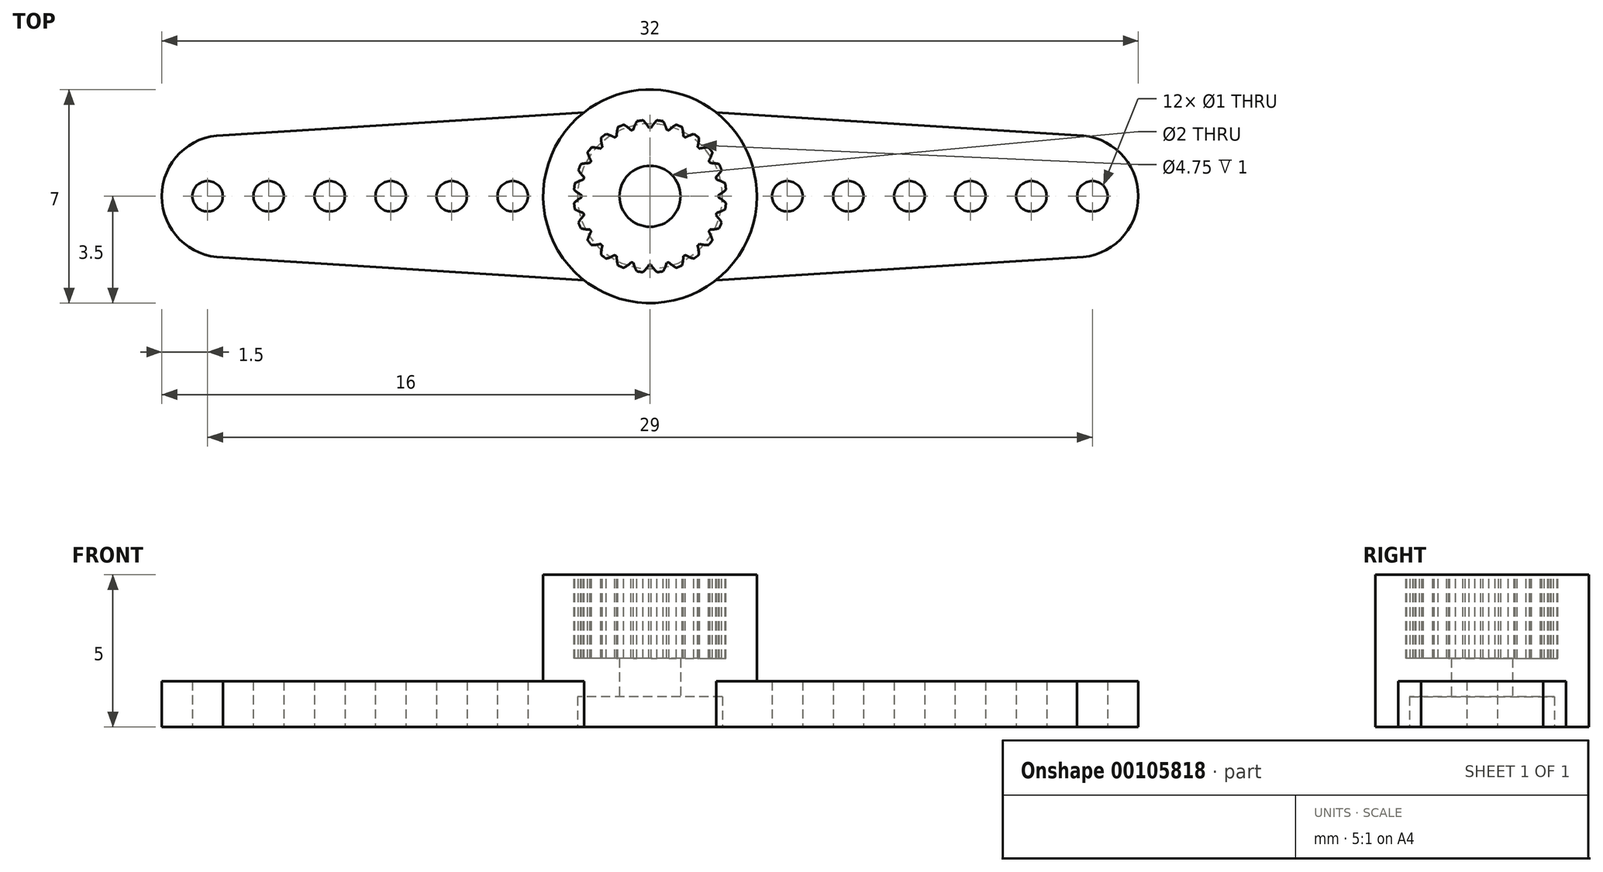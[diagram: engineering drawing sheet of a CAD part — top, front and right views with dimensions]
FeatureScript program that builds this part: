
annotation { "Feature Type Name" : "Feature", "Feature Type Description" : "" }
export const myFeature = defineFeature(function(context is Context, id is Id, definition is map)
    precondition{}
    {
        {
            var Q0;
            Q0=qCreatedBy(makeId("Top.planeOp"),FACE);
            var sketch = newSketch(context, id + "F0", { "sketchPlane" : qUnion([Q0])});
            skCircle(sketch, "E0", {"center": v(0, 0) * mm, "radius": 3.5 * mm});
            skCircle(sketch, "E1", {"center": v(-14, 0) * mm, "radius": 2 * mm});
            skLineSegment(sketch, "E2", {"start": v(-14, 2) * mm, "end": v(-2.17, 2.75) * mm});
            skLineSegment(sketch, "E3", {"start": v(-14, -2) * mm, "end": v(-2.17, -2.75) * mm});
            skCircle(sketch, "E4", {"center": v(0, 0) * mm, "radius": 1 * mm});
            skCircle(sketch, "E5", {"center": v(-14.5, 0) * mm, "radius": 0.5 * mm});
            skLineSegment(sketch, "E6", {"start": v(-16.68, 0) * mm, "end": v(5.78, 0) * mm, "construction": true});
            skCircle(sketch, "E7.1.0.0", {"center": v(-12.5, 0) * mm, "radius": 0.5 * mm});
            skCircle(sketch, "E7.2.0.0", {"center": v(-10.5, 0) * mm, "radius": 0.5 * mm});
            skLineSegment(sketch, "E7.direction1", {"start": v(-14.5, 0) * mm, "end": v(-12.5, 0) * mm, "construction": true});
            skCircle(sketch, "E8.0.3.0", {"center": v(-8.5, 0) * mm, "radius": 0.5 * mm});
            skCircle(sketch, "E8.0.4.0", {"center": v(-6.5, 0) * mm, "radius": 0.5 * mm});
            skCircle(sketch, "E8.0.5.0", {"center": v(-4.5, 0) * mm, "radius": 0.5 * mm});
            skSolve(sketch);
        }
        {
            var Q0;
            {var subQ6=sQuery(id+"F0.wireOp",EDGE,"E2");Q0=makeQuery(id+"F0.imprint","IMPRINT",FACE,{"disambiguationData":[TD([[makeQuery(id+"F0.imprint","IMPRINT",EDGE,{"derivedFrom":subQ6}),-1.0]])]});}
            var Q1;
            Q1=makeQuery(id+"F0.imprint","IMPRINT",FACE,{"disambiguationData":[TD([[makeQuery(id+"F0.imprint","IMPRINT",EDGE,{"derivedFrom":sQuery(id+"F0.wireOp",EDGE,"11ce5147-8903-4a82-81a3-89551e99495c")}),-1.0]])]});
            var Q2;
            Q2=makeQuery(id+"F0.imprint","IMPRINT",FACE,{"disambiguationData":[TD([[makeQuery(id+"F0.imprint","IMPRINT",EDGE,{"derivedFrom":sQuery(id+"F0.wireOp",EDGE,"E4")}),-1.0]])]});
            var Q3;
            Q3=makeQuery(id+"F0.imprint","IMPRINT",FACE,{"disambiguationData":[TD([[makeQuery(id+"F0.imprint","IMPRINT",EDGE,{"derivedFrom":sQuery(id+"F0.wireOp",EDGE,"E5")}),-1.0]])]});
            extrude(context, id + "F1", {"entities" : qUnion([Q0, Q1, Q2, Q3]), "depth" : 1.5 * mm});
        }
        {
            var Q0;
            Q0=makeQuery(id+"F0.imprint","IMPRINT",FACE,{"disambiguationData":[TD([[makeQuery(id+"F0.imprint","IMPRINT",EDGE,{"derivedFrom":sQuery(id+"F0.wireOp",EDGE,"E4")}),-1.0]])]});
            extrude(context, id + "F2", {"entities" : qUnion([Q0]), "operationType" : NewBodyOperationType.ADD, "depth" : 5 * mm});
        }
        {
            var Q0;
            Q0=makeQuery(id+"F0.imprint","IMPRINT",FACE,{"disambiguationData":[TD([[makeQuery(id+"F0.imprint","IMPRINT",EDGE,{"derivedFrom":sQuery(id+"F0.wireOp",EDGE,"E4")}),-1.0]])]});
            var sketch = newSketch(context, id + "F3", { "sketchPlane" : qUnion([Q0])});
            skCircle(sketch, "E9", {"center": v(0, 0) * mm, "radius": 2.37 * mm});
            skSolve(sketch);
        }
        {
            var Q0;
            Q0=qSketchRegion(id+"F3",true);
            extrude(context, id + "F4", {"entities" : qUnion([Q0]), "operationType" : NewBodyOperationType.REMOVE, "depth" : 1 * mm});
        }
        {
            var Q0;
            Q0=makeQuery(id+"F2.opExtrude","CAP_FACE",FACE,{"disambiguationData":[OSD([sQuery(id+"F0.wireOp",EDGE,"E0"),sQuery(id+"F0.wireOp",EDGE,"E4")])],"isStart":false});
            var sketch = newSketch(context, id + "F5", { "sketchPlane" : qUnion([Q0])});
            skCircle(sketch, "E10", {"center": v(0, 0) * mm, "radius": 2.25 * mm});
            skCircle(sketch, "E11", {"center": v(0, 0) * mm, "radius": 2.5 * mm, "construction": true});
            skLineSegment(sketch, "E12", {"start": v(0, 0) * mm, "end": v(0.98, 3.66) * mm, "construction": true});
            skLineSegment(sketch, "E13", {"start": v(0, 0) * mm, "end": v(2.5, 4.33) * mm, "construction": true});
            skArc(sketch, "E14", {"start": v(0.23, 2.49) * mm, "mid": v(0.12, 2.38) * mm, "end": v(0.04, 2.25) * mm});
            skArc(sketch, "E15", {"start": v(0.54, 2.18) * mm, "mid": v(0.5, 2.33) * mm, "end": v(0.43, 2.46) * mm});
            skArc(sketch, "E16", {"start": v(0.43, 2.46) * mm, "mid": v(0.33, 2.48) * mm, "end": v(0.23, 2.49) * mm});
            skCircle(sketch, "E17.2.0", {"center": v(0, 0) * mm, "radius": 2.25 * mm, "construction": true});
            skArc(sketch, "E18.1.1", {"start": v(-0.43, 2.46) * mm, "mid": v(-0.5, 2.33) * mm, "end": v(-0.54, 2.18) * mm});
            skArc(sketch, "E18.1.2", {"start": v(-0.23, 2.49) * mm, "mid": v(-0.33, 2.48) * mm, "end": v(-0.43, 2.46) * mm});
            skArc(sketch, "E18.1.3", {"start": v(-0.04, 2.25) * mm, "mid": v(-0.12, 2.38) * mm, "end": v(-0.23, 2.49) * mm});
            skArc(sketch, "E18.2.1", {"start": v(-1.05, 2.27) * mm, "mid": v(-1.1, 2.12) * mm, "end": v(-1.1, 1.97) * mm});
            skArc(sketch, "E18.2.2", {"start": v(-0.86, 2.35) * mm, "mid": v(-0.96, 2.3) * mm, "end": v(-1.05, 2.27) * mm});
            skArc(sketch, "E18.2.3", {"start": v(-0.62, 2.16) * mm, "mid": v(-0.73, 2.26) * mm, "end": v(-0.86, 2.35) * mm});
            skArc(sketch, "E19.2.3.0", {"start": v(-1.6, 1.92) * mm, "mid": v(-1.6, 1.77) * mm, "end": v(-1.56, 1.62) * mm});
            skArc(sketch, "E19.6.3.0", {"start": v(-1.44, 2.04) * mm, "mid": v(-1.52, 1.98) * mm, "end": v(-1.6, 1.92) * mm});
            skArc(sketch, "E19.10.3.0", {"start": v(-1.16, 1.93) * mm, "mid": v(-1.3, 2) * mm, "end": v(-1.44, 2.04) * mm});
            skArc(sketch, "E19.2.4.0", {"start": v(-2.04, 1.44) * mm, "mid": v(-2, 1.3) * mm, "end": v(-1.93, 1.16) * mm});
            skArc(sketch, "E19.6.4.0", {"start": v(-1.92, 1.6) * mm, "mid": v(-1.98, 1.52) * mm, "end": v(-2.04, 1.44) * mm});
            skArc(sketch, "E19.10.4.0", {"start": v(-1.62, 1.56) * mm, "mid": v(-1.77, 1.6) * mm, "end": v(-1.92, 1.6) * mm});
            skArc(sketch, "E19.2.5.0", {"start": v(-2.35, 0.86) * mm, "mid": v(-2.27, 0.73) * mm, "end": v(-2.16, 0.62) * mm});
            skArc(sketch, "E19.6.5.0", {"start": v(-2.27, 1.05) * mm, "mid": v(-2.3, 0.96) * mm, "end": v(-2.35, 0.86) * mm});
            skArc(sketch, "E19.10.5.0", {"start": v(-1.97, 1.1) * mm, "mid": v(-2.12, 1.08) * mm, "end": v(-2.27, 1.05) * mm});
            skArc(sketch, "E19.2.6.0", {"start": v(-2.49, 0.23) * mm, "mid": v(-2.38, 0.12) * mm, "end": v(-2.25, 0.04) * mm});
            skArc(sketch, "E19.6.6.0", {"start": v(-2.46, 0.43) * mm, "mid": v(-2.48, 0.33) * mm, "end": v(-2.49, 0.23) * mm});
            skArc(sketch, "E19.10.6.0", {"start": v(-2.18, 0.54) * mm, "mid": v(-2.33, 0.5) * mm, "end": v(-2.46, 0.43) * mm});
            skArc(sketch, "E19.2.7.0", {"start": v(-2.46, -0.43) * mm, "mid": v(-2.33, -0.5) * mm, "end": v(-2.18, -0.54) * mm});
            skArc(sketch, "E19.6.7.0", {"start": v(-2.49, -0.22) * mm, "mid": v(-2.48, -0.33) * mm, "end": v(-2.46, -0.43) * mm});
            skArc(sketch, "E19.10.7.0", {"start": v(-2.25, -0.04) * mm, "mid": v(-2.38, -0.12) * mm, "end": v(-2.49, -0.22) * mm});
            skArc(sketch, "E19.2.8.0", {"start": v(-2.27, -1.05) * mm, "mid": v(-2.12, -1.1) * mm, "end": v(-1.97, -1.1) * mm});
            skArc(sketch, "E19.6.8.0", {"start": v(-2.35, -0.86) * mm, "mid": v(-2.3, -0.96) * mm, "end": v(-2.27, -1.05) * mm});
            skArc(sketch, "E19.10.8.0", {"start": v(-2.16, -0.62) * mm, "mid": v(-2.26, -0.73) * mm, "end": v(-2.35, -0.86) * mm});
            skArc(sketch, "E19.2.9.0", {"start": v(-1.92, -1.6) * mm, "mid": v(-1.77, -1.6) * mm, "end": v(-1.62, -1.56) * mm});
            skArc(sketch, "E19.6.9.0", {"start": v(-2.04, -1.44) * mm, "mid": v(-1.98, -1.52) * mm, "end": v(-1.92, -1.6) * mm});
            skArc(sketch, "E19.10.9.0", {"start": v(-1.93, -1.16) * mm, "mid": v(-2, -1.3) * mm, "end": v(-2.04, -1.44) * mm});
            skArc(sketch, "E19.2.10.0", {"start": v(-1.44, -2.04) * mm, "mid": v(-1.3, -2) * mm, "end": v(-1.16, -1.93) * mm});
            skArc(sketch, "E19.6.10.0", {"start": v(-1.6, -1.92) * mm, "mid": v(-1.52, -1.98) * mm, "end": v(-1.44, -2.04) * mm});
            skArc(sketch, "E19.10.10.0", {"start": v(-1.56, -1.62) * mm, "mid": v(-1.6, -1.77) * mm, "end": v(-1.6, -1.92) * mm});
            skArc(sketch, "E19.2.11.0", {"start": v(-0.86, -2.35) * mm, "mid": v(-0.73, -2.27) * mm, "end": v(-0.62, -2.16) * mm});
            skArc(sketch, "E19.6.11.0", {"start": v(-1.05, -2.27) * mm, "mid": v(-0.96, -2.3) * mm, "end": v(-0.86, -2.35) * mm});
            skArc(sketch, "E19.10.11.0", {"start": v(-1.1, -1.97) * mm, "mid": v(-1.08, -2.12) * mm, "end": v(-1.05, -2.27) * mm});
            skArc(sketch, "E19.2.12.0", {"start": v(-0.23, -2.49) * mm, "mid": v(-0.12, -2.38) * mm, "end": v(-0.04, -2.25) * mm});
            skArc(sketch, "E19.6.12.0", {"start": v(-0.43, -2.46) * mm, "mid": v(-0.33, -2.48) * mm, "end": v(-0.23, -2.49) * mm});
            skArc(sketch, "E19.10.12.0", {"start": v(-0.54, -2.18) * mm, "mid": v(-0.5, -2.33) * mm, "end": v(-0.43, -2.46) * mm});
            skArc(sketch, "E19.2.13.0", {"start": v(0.43, -2.46) * mm, "mid": v(0.5, -2.33) * mm, "end": v(0.54, -2.18) * mm});
            skArc(sketch, "E19.6.13.0", {"start": v(0.22, -2.49) * mm, "mid": v(0.33, -2.48) * mm, "end": v(0.43, -2.46) * mm});
            skArc(sketch, "E19.10.13.0", {"start": v(0.04, -2.25) * mm, "mid": v(0.12, -2.38) * mm, "end": v(0.23, -2.49) * mm});
            skArc(sketch, "E19.2.14.0", {"start": v(1.05, -2.27) * mm, "mid": v(1.1, -2.12) * mm, "end": v(1.1, -1.97) * mm});
            skArc(sketch, "E19.6.14.0", {"start": v(0.86, -2.35) * mm, "mid": v(0.96, -2.3) * mm, "end": v(1.05, -2.27) * mm});
            skArc(sketch, "E19.10.14.0", {"start": v(0.62, -2.16) * mm, "mid": v(0.73, -2.26) * mm, "end": v(0.86, -2.35) * mm});
            skArc(sketch, "E19.2.15.0", {"start": v(1.6, -1.92) * mm, "mid": v(1.6, -1.77) * mm, "end": v(1.56, -1.62) * mm});
            skArc(sketch, "E19.6.15.0", {"start": v(1.44, -2.04) * mm, "mid": v(1.52, -1.98) * mm, "end": v(1.6, -1.92) * mm});
            skArc(sketch, "E19.10.15.0", {"start": v(1.16, -1.93) * mm, "mid": v(1.3, -2) * mm, "end": v(1.44, -2.04) * mm});
            skArc(sketch, "E19.2.16.0", {"start": v(2.04, -1.44) * mm, "mid": v(2, -1.3) * mm, "end": v(1.93, -1.16) * mm});
            skArc(sketch, "E19.6.16.0", {"start": v(1.92, -1.6) * mm, "mid": v(1.98, -1.52) * mm, "end": v(2.04, -1.44) * mm});
            skArc(sketch, "E19.10.16.0", {"start": v(1.62, -1.56) * mm, "mid": v(1.77, -1.6) * mm, "end": v(1.92, -1.6) * mm});
            skArc(sketch, "E19.2.17.0", {"start": v(2.35, -0.86) * mm, "mid": v(2.27, -0.73) * mm, "end": v(2.16, -0.62) * mm});
            skArc(sketch, "E19.6.17.0", {"start": v(2.27, -1.05) * mm, "mid": v(2.3, -0.96) * mm, "end": v(2.35, -0.86) * mm});
            skArc(sketch, "E19.10.17.0", {"start": v(1.97, -1.1) * mm, "mid": v(2.12, -1.08) * mm, "end": v(2.27, -1.05) * mm});
            skArc(sketch, "E19.2.18.0", {"start": v(2.49, -0.23) * mm, "mid": v(2.38, -0.12) * mm, "end": v(2.25, -0.04) * mm});
            skArc(sketch, "E19.6.18.0", {"start": v(2.46, -0.43) * mm, "mid": v(2.48, -0.33) * mm, "end": v(2.49, -0.23) * mm});
            skArc(sketch, "E19.10.18.0", {"start": v(2.18, -0.54) * mm, "mid": v(2.33, -0.5) * mm, "end": v(2.46, -0.43) * mm});
            skArc(sketch, "E19.2.19.0", {"start": v(2.46, 0.43) * mm, "mid": v(2.33, 0.5) * mm, "end": v(2.18, 0.54) * mm});
            skArc(sketch, "E19.6.19.0", {"start": v(2.49, 0.22) * mm, "mid": v(2.48, 0.33) * mm, "end": v(2.46, 0.43) * mm});
            skArc(sketch, "E19.10.19.0", {"start": v(2.25, 0.04) * mm, "mid": v(2.38, 0.12) * mm, "end": v(2.49, 0.22) * mm});
            skArc(sketch, "E19.2.20.0", {"start": v(2.27, 1.05) * mm, "mid": v(2.12, 1.1) * mm, "end": v(1.97, 1.1) * mm});
            skArc(sketch, "E19.6.20.0", {"start": v(2.35, 0.86) * mm, "mid": v(2.3, 0.96) * mm, "end": v(2.27, 1.05) * mm});
            skArc(sketch, "E19.10.20.0", {"start": v(2.16, 0.62) * mm, "mid": v(2.26, 0.73) * mm, "end": v(2.35, 0.86) * mm});
            skArc(sketch, "E19.2.21.0", {"start": v(1.92, 1.6) * mm, "mid": v(1.77, 1.6) * mm, "end": v(1.62, 1.56) * mm});
            skArc(sketch, "E19.6.21.0", {"start": v(2.04, 1.44) * mm, "mid": v(1.98, 1.52) * mm, "end": v(1.92, 1.6) * mm});
            skArc(sketch, "E19.10.21.0", {"start": v(1.93, 1.16) * mm, "mid": v(2, 1.3) * mm, "end": v(2.04, 1.44) * mm});
            skArc(sketch, "E19.2.22.0", {"start": v(1.44, 2.04) * mm, "mid": v(1.3, 2) * mm, "end": v(1.16, 1.93) * mm});
            skArc(sketch, "E19.6.22.0", {"start": v(1.6, 1.92) * mm, "mid": v(1.52, 1.98) * mm, "end": v(1.44, 2.04) * mm});
            skArc(sketch, "E19.10.22.0", {"start": v(1.56, 1.62) * mm, "mid": v(1.6, 1.77) * mm, "end": v(1.6, 1.92) * mm});
            skArc(sketch, "E19.2.23.0", {"start": v(0.86, 2.35) * mm, "mid": v(0.73, 2.27) * mm, "end": v(0.62, 2.16) * mm});
            skArc(sketch, "E19.6.23.0", {"start": v(1.05, 2.27) * mm, "mid": v(0.96, 2.3) * mm, "end": v(0.86, 2.35) * mm});
            skArc(sketch, "E19.10.23.0", {"start": v(1.1, 1.97) * mm, "mid": v(1.08, 2.12) * mm, "end": v(1.05, 2.27) * mm});
            skSolve(sketch);
        }
        {
            var Q0;
            Q0=qSketchRegion(id+"F5",true);
            extrude(context, id + "F6", {"entities" : qUnion([Q0]), "operationType" : NewBodyOperationType.REMOVE, "oppositeDirection" : true, "depth" : 2.75 * mm});
        }
        {
            var Q0;
            Q0=makeQuery(id+"F1.opExtrude","SWEPT_BODY",BODY,{"disambiguationData":[OSD([sQuery(id+"F0.wireOp",EDGE,"E0"),sQuery(id+"F0.wireOp",EDGE,"E1"),sQuery(id+"F0.wireOp",EDGE,"E2"),sQuery(id+"F0.wireOp",EDGE,"E3"),sQuery(id+"F0.wireOp",EDGE,"E4"),sQuery(id+"F0.wireOp",EDGE,"E5"),sQuery(id+"F0.wireOp",EDGE,"E7.1.0.0"),sQuery(id+"F0.wireOp",EDGE,"E7.2.0.0"),sQuery(id+"F0.wireOp",EDGE,"E8.0.3.0"),sQuery(id+"F0.wireOp",EDGE,"E8.0.4.0"),sQuery(id+"F0.wireOp",EDGE,"E8.0.5.0")])]});
            var Q1;
            Q1=qCreatedBy(makeId("Right.planeOp"),FACE);
            mirror(context, id + "F7", {"operationType" : NewBodyOperationType.ADD, "entities" : qUnion([Q0]), "mirrorPlane" : qUnion([Q1])});
        }
    });
